# Revit family: RSH_16_18_s200
name_source: partatom
category: Generic Models
units: mm (PartAtom-declared; Revit-internal decimal feet)

## family parameters
Always vertical = No
Can host rebar = Yes
Cut with Voids When Loaded = No
Part Type = Normal
Room Calculation Point = No
Round Connector Dimension = Use Diameter
Shared = No
Work Plane-Based = Yes

## types (4) — shared parameters
CenterToCenter_2 = 210 mm  [stored 0.688976 ft]
Default Elevation = 1219 mm
Manufacturer = Recostal

## per-type parameters (varying)
| type | Diameter Rebar | Length rebar | Model | Width Box | Width rebar |
| RSH 18 - 12 - 200mm | 12 mm  [stored 0.0393701 ft] | 610 mm  [stored 2.00131 ft] | RSH 18_12_200 | 139 mm | 125 mm  [stored 0.410105 ft] |
| RSH 18 - 10 - 200mm | 10 mm  [stored 0.0328084 ft] | 540 mm  [stored 1.77165 ft] | RSH 18_10_200 | 139 mm | 125 mm  [stored 0.410105 ft] |
| RSH 16 - 10 - 200mm | 10 mm  [stored 0.0328084 ft] | 540 mm  [stored 1.77165 ft] | RSH 16_10_200 | 119 mm | 105 mm  [stored 0.344488 ft] |
| RSH 16 - 12 - 200mm | 12 mm  [stored 0.0393701 ft] | 610 mm  [stored 2.00131 ft] | RSH 16_10_200 | 119 mm | 105 mm  [stored 0.344488 ft] |

note: [stored X ft] marks values corroborated as IEEE doubles in the binary element streams (Revit-internal decimal feet)

## geometry (parser evidence)
native form markers: Sweep x36
no freeform markers — native parametric forms only
